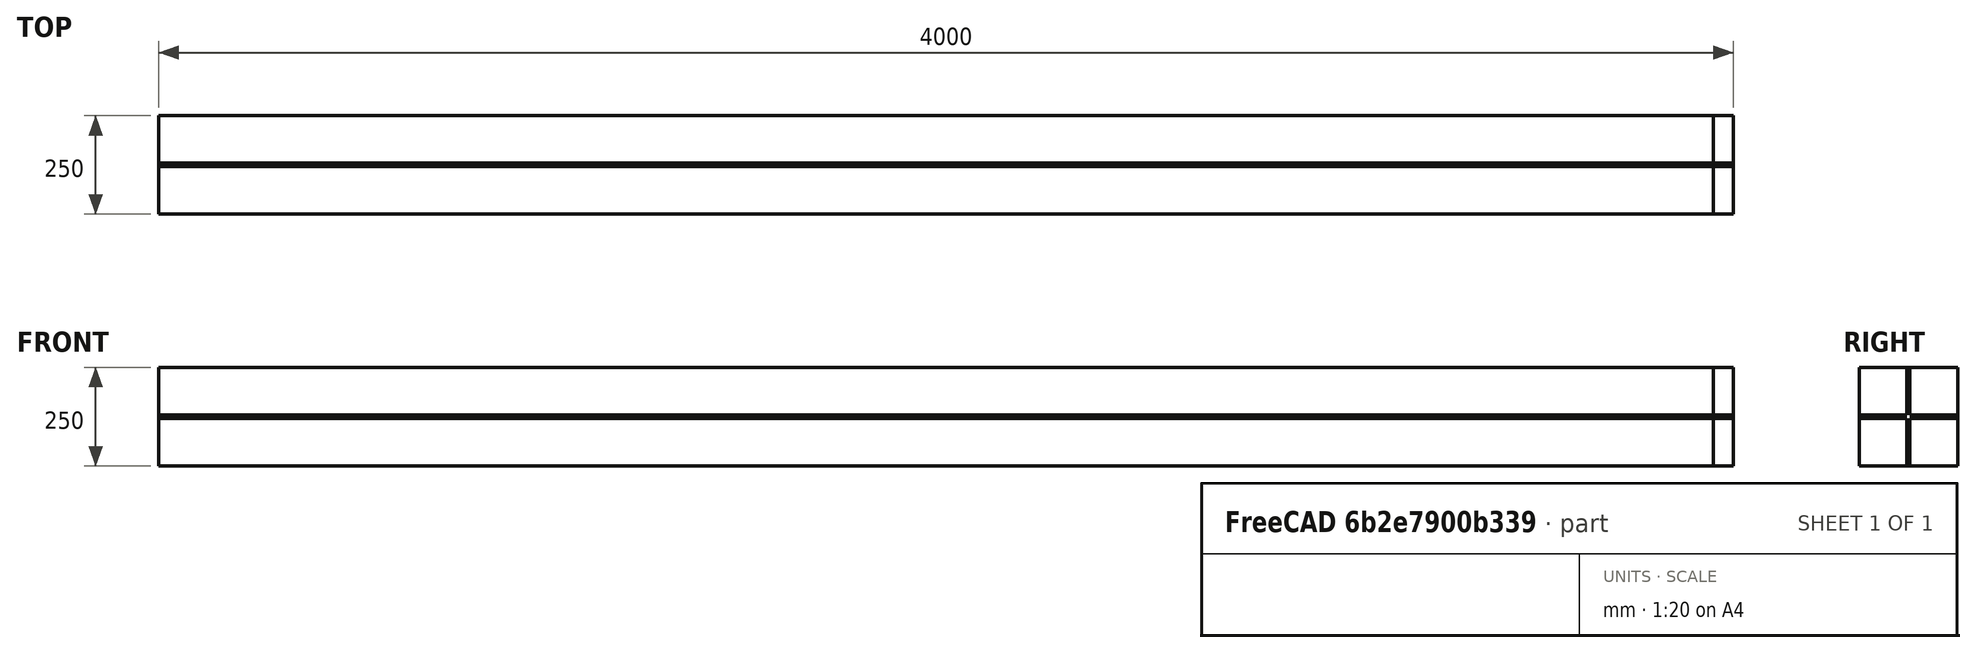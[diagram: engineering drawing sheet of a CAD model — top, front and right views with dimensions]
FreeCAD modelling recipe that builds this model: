
FCSTD DOCUMENT  (FreeCAD 0.21R33694 (Git))
Label: cruciform
License: All rights reserved
LicenseURL: http://en.wikipedia.org/wiki/All_rights_reserved
objects: Fem::ConstraintDisplacement×2, Part::Box×1, App::MaterialObjectPython×1, Fem::FemSolverObjectPython×1, Sketcher::SketchObject×1, Part::Extrusion×1, Part::FeaturePython×1, Fem::FemMeshObjectPython×1, Fem::ConstraintFixed×1, Fem::ConstraintForce×1, Fem::FemAnalysis×1
note: 4 computed .brp shape members not serialized (recipe doc carries the construction recipe); baked Part::Feature solids carry a one-line shape summary decoded from their .brp

FEATURE [Part::Box] Box002  label="Cube002"
  AttacherType = Attacher::AttachEngine3D
  Height = 250
  Length = 50
  Placement = pos=(3950,0,-121) rot=(0,0,1;0rad)
  Width = 250
FEATURE [App::MaterialObjectPython] MaterialSolid  # material (typed FeaturePython)
  Category = 0
  Material = AuthorAndLicense=(c) 2014 M. Münch - GNU Lesser General Public License (LGPL),CardName=Steel-St-E-315,Density=7800 kg/m^3,Father=Metal,+13 more (map truncated)
FEATURE [Fem::FemSolverObjectPython] SolverCcxTools  # FEM object (typed FeaturePython)
  AnalysisType = 0
  BeamShellResultOutput3D = false
  BucklingFactors = 1
  EigenmodeHighLimit = 1000000
  EigenmodeLowLimit = 0
  EigenmodesCount = 10
  GeometricalNonlinearity = 0
  IterationsControlParameterCutb = 0.25,0.5,0.75,0.85,,,1.5,
  IterationsControlParameterIter = 4,8,9,200,10,400,,200,,
  IterationsControlParameterTimeUse = false
  IterationsThermoMechMaximum = 2000
  IterationsUserDefinedIncrementations = false
  IterationsUserDefinedTimeStepLength = false
  MaterialNonlinearity = 0
  MatrixSolverType = 0
  SplitInputWriter = false
  ThermoMechSteadyState = true
  TimeEnd = 1
  TimeInitialStep = 0.01
FEATURE [Sketcher::SketchObject] Sketch
  FullyConstrained = true
  Placement = pos=(0,0,0) rot=(0.57735,0.57735,0.57735;2.0944rad)
  sketch-geometry (12):
    g0: LineSegment StartX=0 StartY=0 StartZ=0 EndX=0 EndY=8 EndZ=0
    g1: LineSegment StartX=0 StartY=8 StartZ=0 EndX=121 EndY=8 EndZ=0
    g2: LineSegment StartX=121 StartY=8 StartZ=0 EndX=121 EndY=129 EndZ=0
    g3: LineSegment StartX=121 StartY=129 StartZ=0 EndX=129 EndY=129 EndZ=0
    g4: LineSegment StartX=129 StartY=129 StartZ=0 EndX=129 EndY=8 EndZ=0
    g5: LineSegment StartX=129 StartY=8 StartZ=0 EndX=250 EndY=8 EndZ=0
    g6: LineSegment StartX=250 StartY=8 StartZ=0 EndX=250 EndY=0 EndZ=0
    g7: LineSegment StartX=250 StartY=0 StartZ=0 EndX=129 EndY=0 EndZ=0
    g8: LineSegment StartX=129 StartY=0 StartZ=0 EndX=129 EndY=-121 EndZ=0
    g9: LineSegment StartX=129 StartY=-121 StartZ=0 EndX=121 EndY=-121 EndZ=0
    g10: LineSegment StartX=121 StartY=-121 StartZ=0 EndX=121 EndY=0 EndZ=0
    g11: LineSegment StartX=121 StartY=0 StartZ=0 EndX=0 EndY=0 EndZ=0
  constraints (35):
    c: Coincident(g-1,g0)
    c: PointOnObject(g0,g-2)
    c: Coincident(g0,g1)
    c: Horizontal(g1)
    c: Coincident(g1,g2)
    c: Vertical(g2)
    c: Coincident(g2,g3)
    c: Coincident(g3,g4)
    c: Vertical(g4)
    c: Coincident(g4,g5)
    c: Horizontal(g5)
    c: Coincident(g5,g6)
    c: PointOnObject(g6,g-1)
    c: Coincident(g6,g7)
    c: PointOnObject(g7,g-1)
    c: Coincident(g7,g8)
    c: Coincident(g8,g9)
    c: Coincident(g9,g10)
    c: PointOnObject(g10,g-1)
    c: Vertical(g10)
    c: Coincident(g10,g11)
    c: Coincident(g11,g0)
    c: Vertical(g8)
    c: DistanceY(g0,g0) = 8
    c: DistanceY(g6,g6) = 8
    c: DistanceX(g3,g3) = 8
    c: DistanceX(g9,g9) = 8
    c: Horizontal(g3)
    c: Horizontal(g9)
    c: Vertical(g6)
    c: DistanceX(g1,g1) = 121
    c: DistanceX(g5,g5) = 121
    c: DistanceY(g2,g2) = 121
    c: DistanceY(g10,g10) = 121
    c: DistanceX(g7,g7) = 121
FEATURE [Part::Extrusion] Extrude
  Base = -> Sketch
  Dir = (1,0,0)
  DirMode = 2
  FaceMakerClass = Part::FaceMakerBullseye
  LengthFwd = 4000
  LengthRev = 0
  Solid = true
  Symmetric = false
FEATURE [Part::FeaturePython] BooleanFragments  # WARN: FeaturePython — macro-defined, semantics opaque (R4)
  Mode = 2
  Objects = -> [Box002,Extrude]
  Tolerance = 0
FEATURE [Fem::FemMeshObjectPython] FEMMeshGmsh  # FEM object (typed FeaturePython)
  Algorithm2D = 0
  Algorithm3D = 0
  CharacteristicLengthMax = 80
  CharacteristicLengthMin = 0
  CoherenceMesh = true
  ElementDimension = 0
  ElementOrder = 1
  GeometryTolerance = 1e-06
  GroupsOfNodes = false
  HighOrderOptimize = 0
  MeshSizeFromCurvature = 12
  OptimizeNetgen = false
  OptimizeStd = true
  Part = -> BooleanFragments
  RecombinationAlgorithm = 0
  Recombine3DAll = false
  RecombineAll = false
  SecondOrderLinear = false
FEATURE [Fem::ConstraintFixed] ConstraintFixed
  NormalDirection = (-1,0,0)
  References = -> [BooleanFragments]
  Scale = 17
FEATURE [Fem::ConstraintDisplacement] ConstraintDisplacement
  NormalDirection = (0,0,1)
  Normals = (32) [(0,0,1),(0,0,1),(0,0,1),(0,0,1),(0,0,1),(0,0,1),(0,0,1),(0,0,1),(0,0,1),(0,0,1),(0,0,1),(0,0,1),(0,0,1),(0,0,1),(0,0,1),(0,0,1),(0,0,1),(0,0,1),+14 more]
  Points = (32) [(3950,129,129),(3966.67,129,129),(3983.33,129,129),(4000,129,129),(3950,169.333,129),(3966.67,169.333,129),(3983.33,169.333,129),(4000,169.333,129),+24 more]
  References = -> [BooleanFragments]
  Scale = 9
  hasXFormula = false
  hasYFormula = false
  hasZFormula = false
  rotxFix = false
  rotxFree = true
  rotyFix = false
  rotyFree = true
  rotzFix = false
  rotzFree = true
  useFlowSurfaceForce = false
  xDisplacement = 0
  xFix = false
  xFree = true
  xRotation = 0
  yDisplacement = 0
  yFix = false
  yFree = true
  yRotation = 0
  zDisplacement = 0
  zFix = false
  zFree = false
  zRotation = 0
FEATURE [Fem::ConstraintDisplacement] ConstraintDisplacement001
  NormalDirection = (0,1,0)
  Normals = (32) [(0,1,0),(0,1,0),(0,1,0),(0,1,0),(0,1,0),(0,1,0),(0,1,0),(0,1,0),(0,1,0),(0,1,0),(0,1,0),(0,1,0),(0,1,0),(0,1,0),(0,1,0),(0,1,0),(0,1,0),(0,1,0),+14 more]
  Points = (32) [(3950,250,-121),(3950,250,-80.6667),(3950,250,-40.3333),(3950,250,0),(3966.67,250,-121),(3966.67,250,-80.6667),(3966.67,250,-40.3333),(3966.67,250,0),+24 more]
  References = -> [BooleanFragments]
  Scale = 9
  hasXFormula = false
  hasYFormula = false
  hasZFormula = false
  rotxFix = false
  rotxFree = true
  rotyFix = false
  rotyFree = true
  rotzFix = false
  rotzFree = true
  useFlowSurfaceForce = false
  xDisplacement = 0
  xFix = false
  xFree = true
  xRotation = 0
  yDisplacement = 0
  yFix = false
  yFree = false
  yRotation = 0
  zDisplacement = 0
  zFix = false
  zFree = true
  zRotation = 0
FEATURE [Fem::ConstraintForce] ConstraintForce
  DirectionVector = (-1,0,0)
  Force = 1000000
  NormalDirection = (1,0,0)
  Points = (64) [(4000,121,-121),(4000,121,-80.6667),(4000,121,-40.3333),(4000,121,0),(4000,80.6667,-121),(4000,80.6667,-80.6667),(4000,80.6667,-40.3333),+57 more]
  References = -> [BooleanFragments]
  Reversed = true
  Scale = 11
FEATURE [Fem::FemAnalysis] Analysis
  Group = -> [FEMMeshGmsh,MaterialSolid,SolverCcxTools,ConstraintFixed,ConstraintDisplacement,ConstraintDisplacement001,ConstraintForce]
